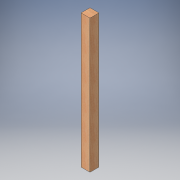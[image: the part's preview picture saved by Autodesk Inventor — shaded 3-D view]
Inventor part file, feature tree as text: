
AUTODESK INVENTOR PART (.ipt)
format: ipt  version: 2016 (Build 200138000, 138)  size: 96,256 bytes
history: native  units: in
note: dims shown in document units (in); Inventor stores cm internally (conversion verified against a paired STEP export)
features: extrude x1, sketch x1
ambient origin geometry x8: Origin, YZ Plane, XZ Plane, XY Plane, X Axis, Y Axis, Z Axis, Center Point
bodies: Solid1 (feature_tree)
feature tree (2):
  extrude  "Extrusion1"  Depth=52.25in TaperAngle=0.0deg
  sketch  "Sketch1"  dims[d0=3.5in d1=52.25in d2=0.0in]
